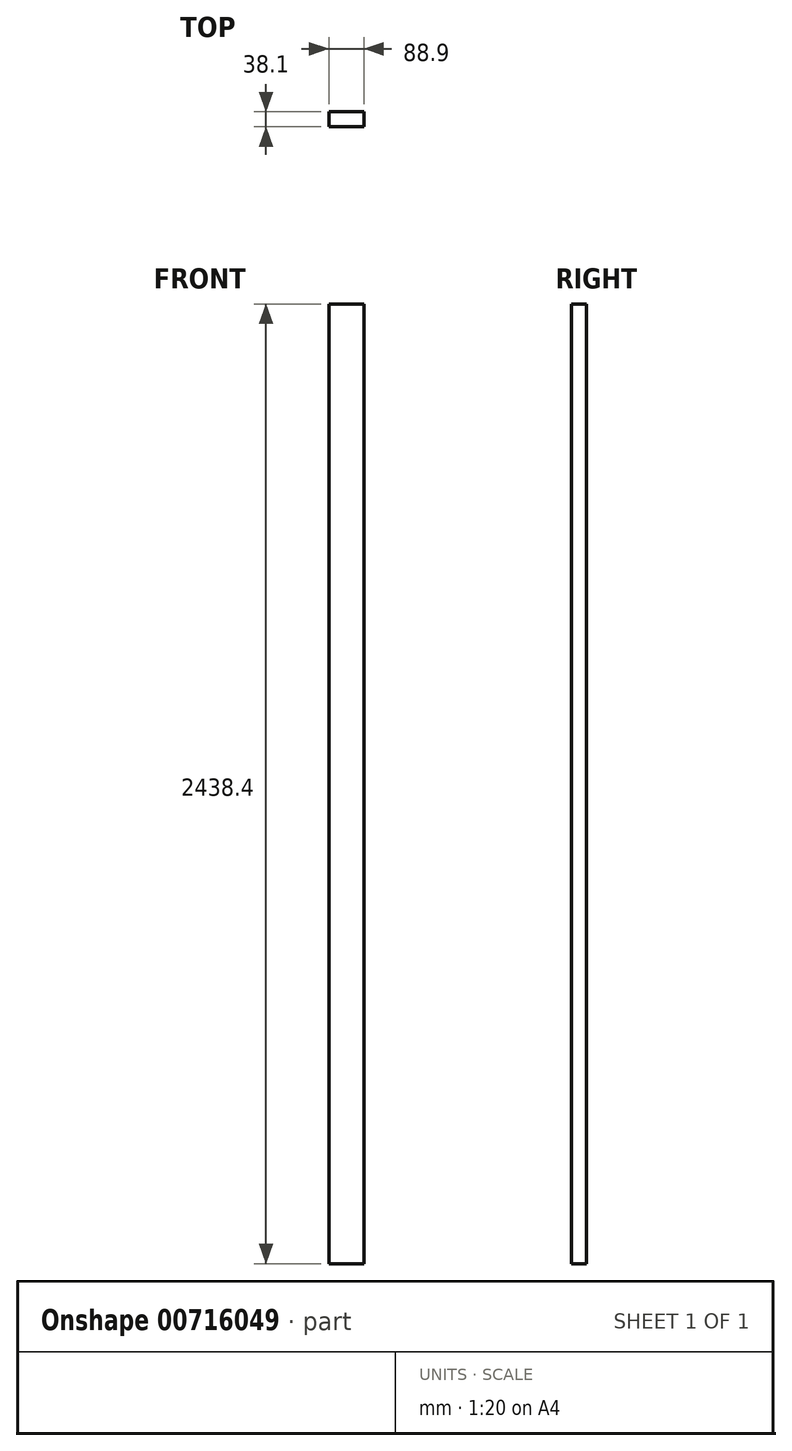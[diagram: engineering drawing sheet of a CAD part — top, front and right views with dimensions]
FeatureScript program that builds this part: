
annotation { "Feature Type Name" : "Feature", "Feature Type Description" : "" }
export const myFeature = defineFeature(function(context is Context, id is Id, definition is map)
    precondition{}
    {
        {
            var Q0;
            Q0=qCreatedBy(makeId("Top.planeOp"),FACE);
            var sketch = newSketch(context, id + "F0", { "sketchPlane" : qUnion([Q0])});
            skLineSegment(sketch, "E0.bottom", {"start": v(-44.45, 19.05) * mm, "end": v(44.45, 19.05) * mm});
            skLineSegment(sketch, "E0.top", {"start": v(-44.45, -19.05) * mm, "end": v(44.45, -19.05) * mm});
            skLineSegment(sketch, "E0.left", {"start": v(-44.45, 19.05) * mm, "end": v(-44.45, -19.05) * mm});
            skLineSegment(sketch, "E0.right", {"start": v(44.45, 19.05) * mm, "end": v(44.45, -19.05) * mm});
            skLineSegment(sketch, "E1", {"start": v(0, 0) * mm, "end": v(83.66, 0) * mm, "construction": true});
            skLineSegment(sketch, "E2", {"start": v(0, 0) * mm, "end": v(0, 50.13) * mm, "construction": true});
            skSolve(sketch);
        }
        {
            var Q0;
            Q0=makeQuery(id+"F0.imprint","IMPRINT",FACE,{"disambiguationData":[TD([[makeQuery(id+"F0.imprint","IMPRINT",EDGE,{"derivedFrom":sQuery(id+"F0.wireOp",EDGE,"E0.bottom")}),-1.0]])]});
            extrude(context, id + "F1", {"entities" : qUnion([Q0]), "depth" : -2438.4 * mm, "offsetDistance" : 25.4 * mm});
        }
    });
